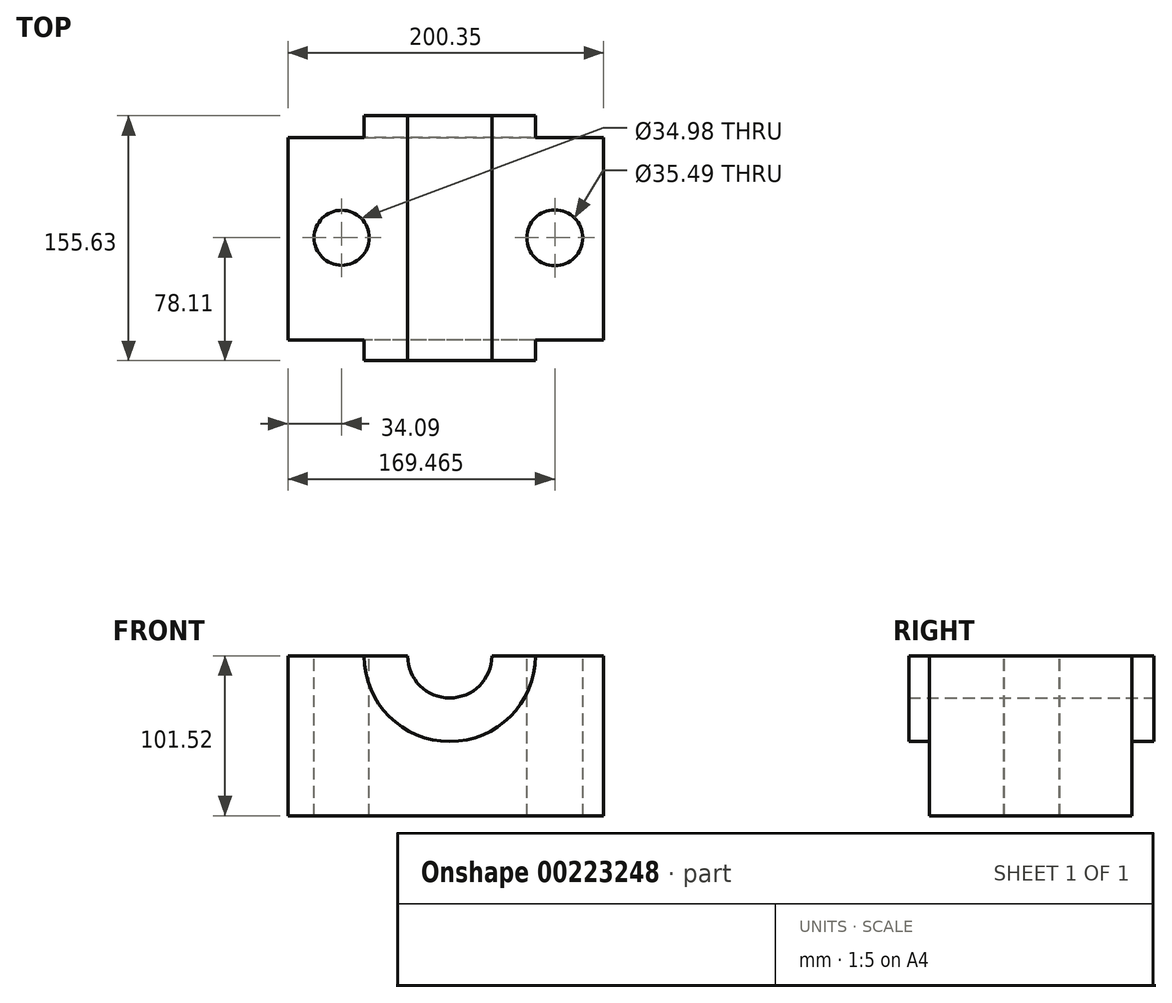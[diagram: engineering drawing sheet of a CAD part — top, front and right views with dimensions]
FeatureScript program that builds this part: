
annotation { "Feature Type Name" : "Feature", "Feature Type Description" : "" }
export const myFeature = defineFeature(function(context is Context, id is Id, definition is map)
    precondition{}
    {
        {
            var Q0;
            Q0=qCreatedBy(makeId("Top.planeOp"),FACE);
            var sketch = newSketch(context, id + "F9", { "sketchPlane" : qUnion([Q0])});
            skCircle(sketch, "E0", {"center": v(-49.24, 0) * mm, "radius": 14.34 * mm});
            skLineSegment(sketch, "E1.bottom", {"start": v(-49.24, 0) * mm, "end": v(-49.24, 0) * mm});
            skLineSegment(sketch, "E1.top", {"start": v(-49.24, 0) * mm, "end": v(-49.24, 0) * mm});
            skLineSegment(sketch, "E1.left", {"start": v(-49.24, 0) * mm, "end": v(-49.24, 0) * mm});
            skLineSegment(sketch, "E1.right", {"start": v(-49.24, 0) * mm, "end": v(-49.24, 0) * mm});
            skLineSegment(sketch, "E2.bottom", {"start": v(-70.84, -37.7) * mm, "end": v(-27.64, -37.7) * mm});
            skLineSegment(sketch, "E2.top", {"start": v(-70.84, 37.7) * mm, "end": v(-27.64, 37.7) * mm});
            skLineSegment(sketch, "E2.left", {"start": v(-70.84, -37.7) * mm, "end": v(-70.84, 37.7) * mm});
            skLineSegment(sketch, "E2.right", {"start": v(-27.64, -37.7) * mm, "end": v(-27.64, 37.7) * mm});
            skLineSegment(sketch, "E3.bottom", {"start": v(-27.64, -37.7) * mm, "end": v(-70.84, -37.7) * mm});
            skLineSegment(sketch, "E3.top", {"start": v(-27.64, 37.7) * mm, "end": v(-70.84, 37.7) * mm});
            skLineSegment(sketch, "E4.bottom", {"start": v(-27.64, 77.52) * mm, "end": v(0, 77.52) * mm});
            skLineSegment(sketch, "E4.top", {"start": v(-27.64, -78.1) * mm, "end": v(0, -78.1) * mm});
            skLineSegment(sketch, "E4.left", {"start": v(-27.64, 77.52) * mm, "end": v(-27.64, -78.1) * mm});
            skLineSegment(sketch, "E4.right", {"start": v(0, 77.52) * mm, "end": v(0, -78.1) * mm});
            skSolve(sketch);
        }
        {
            var Q0;
            Q0=qCreatedBy(makeId("Top.planeOp"),FACE);
            var sketch = newSketch(context, id + "F10", { "sketchPlane" : qUnion([Q0])});
            skLineSegment(sketch, "E5.bottom", {"start": v(0, 77.1) * mm, "end": v(26.73, 77.1) * mm});
            skLineSegment(sketch, "E5.top", {"start": v(0, -78.28) * mm, "end": v(26.73, -78.28) * mm});
            skLineSegment(sketch, "E5.left", {"start": v(0, 77.1) * mm, "end": v(0, -78.28) * mm});
            skLineSegment(sketch, "E5.right", {"start": v(26.73, 77.1) * mm, "end": v(26.73, -78.28) * mm});
            skSolve(sketch);
        }
        {
            var Q0;
            {var subQ3=sQuery(id+"F9.wireOp",EDGE,"E4.bottom");Q0=makeQuery(id+"F9.imprint","IMPRINT",FACE,{"disambiguationData":[TD([[makeQuery(id+"F9.imprint","IMPRINT",EDGE,{"derivedFrom":subQ3}),-1.0]])]});}
            var Q1;
            Q1=makeQuery(id+"F9.imprint","IMPRINT",FACE,{"disambiguationData":[TD([[makeQuery(id+"F9.imprint","IMPRINT",EDGE,{"derivedFrom":sQuery(id+"F9.wireOp",EDGE,"E0")}),-1.0]])]});
            var Q2;
            Q2=sQuery(id+"F10.wireOp",EDGE,"E5.right");
            revolve(context, id + "F0", {"entities" : qUnion([Q0, Q1]), "axis" : qUnion([Q2]), "revolveType" : RevolveType.FULL});
        }
        {
            var Q0;
            Q0=makeQuery(id+"F0.opRevolve","SWEPT_FACE",FACE,{"disambiguationData":[OSD([sQuery(id+"F9.wireOp",EDGE,"E4.top")])]});
            var sketch = newSketch(context, id + "F1", { "sketchPlane" : qUnion([Q0])});
            skLineSegment(sketch, "E6", {"start": v(-91.23, 0) * mm, "end": v(155.72, 0) * mm});
            skLineSegment(sketch, "E7", {"start": v(155.72, 0) * mm, "end": v(155.72, 112.2) * mm});
            skLineSegment(sketch, "E8", {"start": v(155.72, 112.2) * mm, "end": v(-91.23, 112.2) * mm});
            skLineSegment(sketch, "E9", {"start": v(-91.23, 112.2) * mm, "end": v(-91.23, 0) * mm});
            skSolve(sketch);
        }
        {
            var Q0;
            {var subQ0=sQuery(id+"F1.wireOp",EDGE,"E6");var subQ1=sQuery(id+"F9.wireOp",EDGE,"E4.top");var subQ2=makeQuery(id+"F0.opRevolve","SWEPT_EDGE",EDGE,{"disambiguationData":[OSD([subQ1,sQuery(id+"F9.wireOp",EDGE,"E4.left")])]});var subQ3=makeQuery(id+"F1.imprint","INTERSECT",VERTEX,{"disambiguationData":[OD(0.0)],"derivedFrom":[subQ2,subQ0]});Q0=makeQuery(id+"F1.imprint","IMPRINT",FACE,{"disambiguationData":[TD([[makeQuery(id+"F1.imprint","IMPRINT",EDGE,{"disambiguationData":[TD([[subQ3,-1.0]])],"derivedFrom":subQ0}),1.0]])]});}
            var Q1;
            {var subQ0=sQuery(id+"F1.wireOp",EDGE,"E7");Q1=makeQuery(id+"F1.imprint","IMPRINT",FACE,{"disambiguationData":[TD([[makeQuery(id+"F1.imprint","IMPRINT",EDGE,{"derivedFrom":subQ0}),1.0]])]});}
            extrude(context, id + "F2", {"entities" : qUnion([Q0, Q1]), "operationType" : NewBodyOperationType.REMOVE, "endBound" : BoundingType.THROUGH_ALL, "oppositeDirection" : true, "depth" : 25.4 * mm});
        }
        {
            var Q0;
            Q0=qCreatedBy(makeId("Right.planeOp"),FACE);
            var sketch = newSketch(context, id + "F3", { "sketchPlane" : qUnion([Q0])});
            skLineSegment(sketch, "E10", {"start": v(-64.93, 0) * mm, "end": v(-64.93, -101.52) * mm});
            skLineSegment(sketch, "E11", {"start": v(-64.93, -101.52) * mm, "end": v(63.6, -101.52) * mm});
            skLineSegment(sketch, "E12", {"start": v(63.6, -101.52) * mm, "end": v(63.6, 0) * mm});
            skLineSegment(sketch, "E13", {"start": v(63.6, 0) * mm, "end": v(-64.93, 0) * mm});
            skSolve(sketch);
        }
        {
            var Q0;
            Q0=makeQuery(id+"F3.imprint","IMPRINT",FACE,{"disambiguationData":[TD([[makeQuery(id+"F3.imprint","IMPRINT",EDGE,{"derivedFrom":sQuery(id+"F3.wireOp",EDGE,"E10")}),1.0]])]});
            extrude(context, id + "F4", {"entities" : qUnion([Q0]), "operationType" : NewBodyOperationType.ADD, "endBound" : BoundingType.SYMMETRIC, "depth" : 248.7 * mm});
        }
        {
            var Q0;
            {var subQ0=sQuery(id+"F1.wireOp",EDGE,"E6");var subQ1=sQuery(id+"F9.wireOp",EDGE,"E4.top");var subQ2=makeQuery(id+"F0.opRevolve","SWEPT_EDGE",EDGE,{"disambiguationData":[OSD([subQ1,sQuery(id+"F9.wireOp",EDGE,"E4.left")])]});var subQ3=makeQuery(id+"F1.imprint","INTERSECT",VERTEX,{"disambiguationData":[OD(1.0)],"derivedFrom":[subQ2,subQ0]});var subQ5=makeQuery(id+"F1.imprint","INTERSECT",VERTEX,{"disambiguationData":[OD(0.0)],"derivedFrom":[subQ2,subQ0]});Q0=makeQuery(id+"F4.boolean.opBoolean","MERGE",FACE,{"derivedFrom":[makeQuery(id+"F2.boolean.opBoolean","COPY",FACE,{"derivedFrom":makeQuery(id+"F2.opExtrude","SWEPT_FACE",FACE,{"disambiguationData":[OSD([subQ0]),TDD([makeQuery(id+"F1.imprint","IMPRINT",EDGE,{"disambiguationData":[TD([[makeQuery(id+"F1.imprint","INTERSECT",VERTEX,{"derivedFrom":[subQ0,sQuery(id+"F1.wireOp",EDGE,"E9")]}),-1.0]])],"derivedFrom":subQ0}),makeQuery(id+"F1.imprint","IMPRINT",EDGE,{"disambiguationData":[TD([[subQ5,-1.0]])],"derivedFrom":subQ0})])]})}),makeQuery(id+"F2.boolean.opBoolean","COPY",FACE,{"derivedFrom":makeQuery(id+"F2.opExtrude","SWEPT_FACE",FACE,{"disambiguationData":[OSD([subQ0]),TDD([makeQuery(id+"F1.imprint","IMPRINT",EDGE,{"disambiguationData":[TD([[subQ3,1.0]])],"derivedFrom":subQ0}),makeQuery(id+"F1.imprint","IMPRINT",EDGE,{"disambiguationData":[TD([[makeQuery(id+"F1.imprint","INTERSECT",VERTEX,{"derivedFrom":[subQ0,sQuery(id+"F1.wireOp",EDGE,"E7")]}),1.0]])],"derivedFrom":subQ0})])]})}),makeQuery(id+"F4.opExtrude","SWEPT_FACE",FACE,{"disambiguationData":[OSD([sQuery(id+"F3.wireOp",EDGE,"E13")])]})]});}
            var sketch = newSketch(context, id + "F5", { "sketchPlane" : qUnion([Q0])});
            skLineSegment(sketch, "E14", {"start": v(-76, 63.6) * mm, "end": v(-76, -64.93) * mm});
            skLineSegment(sketch, "E15", {"start": v(-76, -64.93) * mm, "end": v(-124.35, -64.93) * mm});
            skLineSegment(sketch, "E16", {"start": v(-124.35, 63.6) * mm, "end": v(-76, 63.6) * mm});
            skSolve(sketch);
        }
        {
            var Q0;
            Q0=makeQuery(id+"F5.imprint","IMPRINT",FACE,{"disambiguationData":[TD([[makeQuery(id+"F5.imprint","IMPRINT",EDGE,{"derivedFrom":sQuery(id+"F5.wireOp",EDGE,"E14")}),-1.0]])]});
            extrude(context, id + "F11", {"entities" : qUnion([Q0]), "operationType" : NewBodyOperationType.REMOVE, "endBound" : BoundingType.THROUGH_ALL, "oppositeDirection" : true, "depth" : 25.4 * mm});
        }
        {
            var Q0;
            {var subQ0=sQuery(id+"F9.wireOp",EDGE,"E4.right");Q0=makeQuery(id+"F4.boolean.opBoolean","SPLIT",FACE,{"disambiguationData":[TD([makeQuery(id+"F0.opRevolve","SWEPT_FACE",FACE,{"disambiguationData":[OSD([subQ0])]})])],"derivedFrom":makeQuery(id+"F4.opExtrude","SWEPT_FACE",FACE,{"disambiguationData":[OSD([sQuery(id+"F3.wireOp",EDGE,"E12")])]})});}
            extrude(context, id + "F6", {"entities" : qUnion([Q0]), "operationType" : NewBodyOperationType.REMOVE, "endBound" : BoundingType.THROUGH_ALL, "oppositeDirection" : true, "depth" : 25.4 * mm});
        }
        {
            var Q0;
            {var subQ0=sQuery(id+"F9.wireOp",EDGE,"E4.left");var subQ1=sQuery(id+"F9.wireOp",EDGE,"E4.top");var subQ5=sQuery(id+"F1.wireOp",EDGE,"E6");var subQ6=makeQuery(id+"F0.opRevolve","SWEPT_EDGE",EDGE,{"disambiguationData":[OSD([subQ1,subQ0])]});var subQ7=makeQuery(id+"F1.imprint","INTERSECT",VERTEX,{"disambiguationData":[OD(1.0)],"derivedFrom":[subQ6,subQ5]});var subQ9=makeQuery(id+"F1.imprint","INTERSECT",VERTEX,{"disambiguationData":[OD(0.0)],"derivedFrom":[subQ6,subQ5]});Q0=makeQuery(id+"F6.boolean.opBoolean","SPLIT",FACE,{"disambiguationData":[TD([makeQuery(id+"F11.boolean.opBoolean","COPY",FACE,{"derivedFrom":makeQuery(id+"F11.opExtrude","SWEPT_FACE",FACE,{"disambiguationData":[OSD([sQuery(id+"F5.wireOp",EDGE,"E14")])]})})])],"derivedFrom":makeQuery(id+"F4.boolean.opBoolean","MERGE",FACE,{"derivedFrom":[makeQuery(id+"F2.boolean.opBoolean","COPY",FACE,{"derivedFrom":makeQuery(id+"F2.opExtrude","SWEPT_FACE",FACE,{"disambiguationData":[OSD([subQ5]),TDD([makeQuery(id+"F1.imprint","IMPRINT",EDGE,{"disambiguationData":[TD([[makeQuery(id+"F1.imprint","INTERSECT",VERTEX,{"derivedFrom":[subQ5,sQuery(id+"F1.wireOp",EDGE,"E9")]}),-1.0]])],"derivedFrom":subQ5}),makeQuery(id+"F1.imprint","IMPRINT",EDGE,{"disambiguationData":[TD([[subQ9,-1.0]])],"derivedFrom":subQ5})])]})}),makeQuery(id+"F2.boolean.opBoolean","COPY",FACE,{"derivedFrom":makeQuery(id+"F2.opExtrude","SWEPT_FACE",FACE,{"disambiguationData":[OSD([subQ5]),TDD([makeQuery(id+"F1.imprint","IMPRINT",EDGE,{"disambiguationData":[TD([[subQ7,1.0]])],"derivedFrom":subQ5}),makeQuery(id+"F1.imprint","IMPRINT",EDGE,{"disambiguationData":[TD([[makeQuery(id+"F1.imprint","INTERSECT",VERTEX,{"derivedFrom":[subQ5,sQuery(id+"F1.wireOp",EDGE,"E7")]}),1.0]])],"derivedFrom":subQ5})])]})}),makeQuery(id+"F4.opExtrude","SWEPT_FACE",FACE,{"disambiguationData":[OSD([sQuery(id+"F3.wireOp",EDGE,"E13")])]})]})});}
            var sketch = newSketch(context, id + "F7", { "sketchPlane" : qUnion([Q0])});
            skCircle(sketch, "E17", {"center": v(-41.9, 0) * mm, "radius": 17.5 * mm});
            skCircle(sketch, "E18", {"center": v(93.46, 0) * mm, "radius": 17.75 * mm});
            skSolve(sketch);
        }
        {
            var Q0;
            Q0=makeQuery(id+"F7.imprint","IMPRINT",FACE,{"disambiguationData":[TD([[makeQuery(id+"F7.imprint","IMPRINT",EDGE,{"derivedFrom":sQuery(id+"F7.wireOp",EDGE,"E18")}),1.0]])]});
            var Q1;
            Q1=makeQuery(id+"F7.imprint","IMPRINT",FACE,{"disambiguationData":[TD([[makeQuery(id+"F7.imprint","IMPRINT",EDGE,{"derivedFrom":sQuery(id+"F7.wireOp",EDGE,"E17")}),1.0]])]});
            extrude(context, id + "F8", {"entities" : qUnion([Q0, Q1]), "operationType" : NewBodyOperationType.REMOVE, "endBound" : BoundingType.THROUGH_ALL, "oppositeDirection" : true, "depth" : 25.4 * mm});
        }
    });
